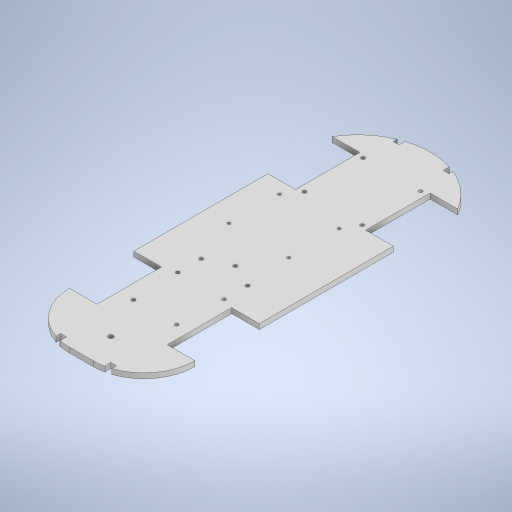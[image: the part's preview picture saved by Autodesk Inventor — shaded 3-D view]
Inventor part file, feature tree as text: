
AUTODESK INVENTOR PART (.ipt)
format: ipt  version: 2024 (Build 280153000, 153)  size: 419,328 bytes
history: native  units: mm
features: extrude x7, sketch x3
ambient origin geometry x8: Origin, YZ Plane, XZ Plane, XY Plane, X Axis, Y Axis, Z Axis, Center Point
bodies: Solid1 (feature_tree)
feature tree (10):
  extrude  "Extrusion1"  Depth=122.0mm
  sketch  "Boceto2"  dims[d2=49.5mm d4=26.8mm]
  sketch  "Boceto3"  dims[d5=62.5mm d6=130.4mm d7=26.8mm d8=62.5mm d9=26.8mm d10=62.5mm d11=26.8mm d12=62.5mm d13=70.9mm d14=5.0mm d15=0.0mm d16=10.0mm d18=38.0mm d19=35.0mm d21=38.0mm d29=5.6mm d30=6.0mm d36=5.6mm d44=5.6mm d45=6.0mm d46=5.6mm d47=6.0mm d69=56.0mm d70=85.0mm d74=1.0mm d75=0.0mm d78=20.0mm d79=0.0mm d122=10.0mm d123=0.0mm d128=16.5mm d133=3.0mm d134=3.5mm d135=3.5mm d136=78.0mm d137=41.9mm d138=3.5mm d139=3.0mm d140=27.5mm d141=55.0mm d142=37.8mm d143=3.2mm d144=5.7mm d146=1.75mm d147=1.75mm d148=3.5mm d149=4.95mm d150=7.45mm d151=3.5mm d152=3.5mm d153=3.5mm d154=5.0mm d155=0.0mm d156=19.0mm d157=35.0mm d158=90.0deg d159=43.0mm d160=43.0mm d161=4.6mm d162=5.0mm d163=0.0mm d164=3.5mm d165=3.5mm d166=58.0mm d167=49.0mm d168=58.0mm d169=90.0deg d170=2.8mm d171=2.8mm d172=2.8mm d173=2.8mm d174=2.2mm d175=2.2mm d176=62.5mm d177=64.0mm d178=4.0mm d179=3.0mm d180=56.0mm d181=57.0mm d182=3.5mm d183=3.5mm d184=3.5mm d185=3.5mm d186=10.0mm d187=0.0mm]
  extrude  "Extrusión2"  Depth=26.8mm
  extrude  "Extrusión4"  Depth=130.4mm
  extrude  "Extrusión6"  Depth=26.8mm
  extrude  "Extrusión7"  Depth=62.5mm
  extrude  "Extrusión8"  Depth=26.8mm
  extrude  "Extrusión9"  Depth=62.5mm
  sketch  "Sketch1"  dims[d0=122.0mm d1=390.0mm]
